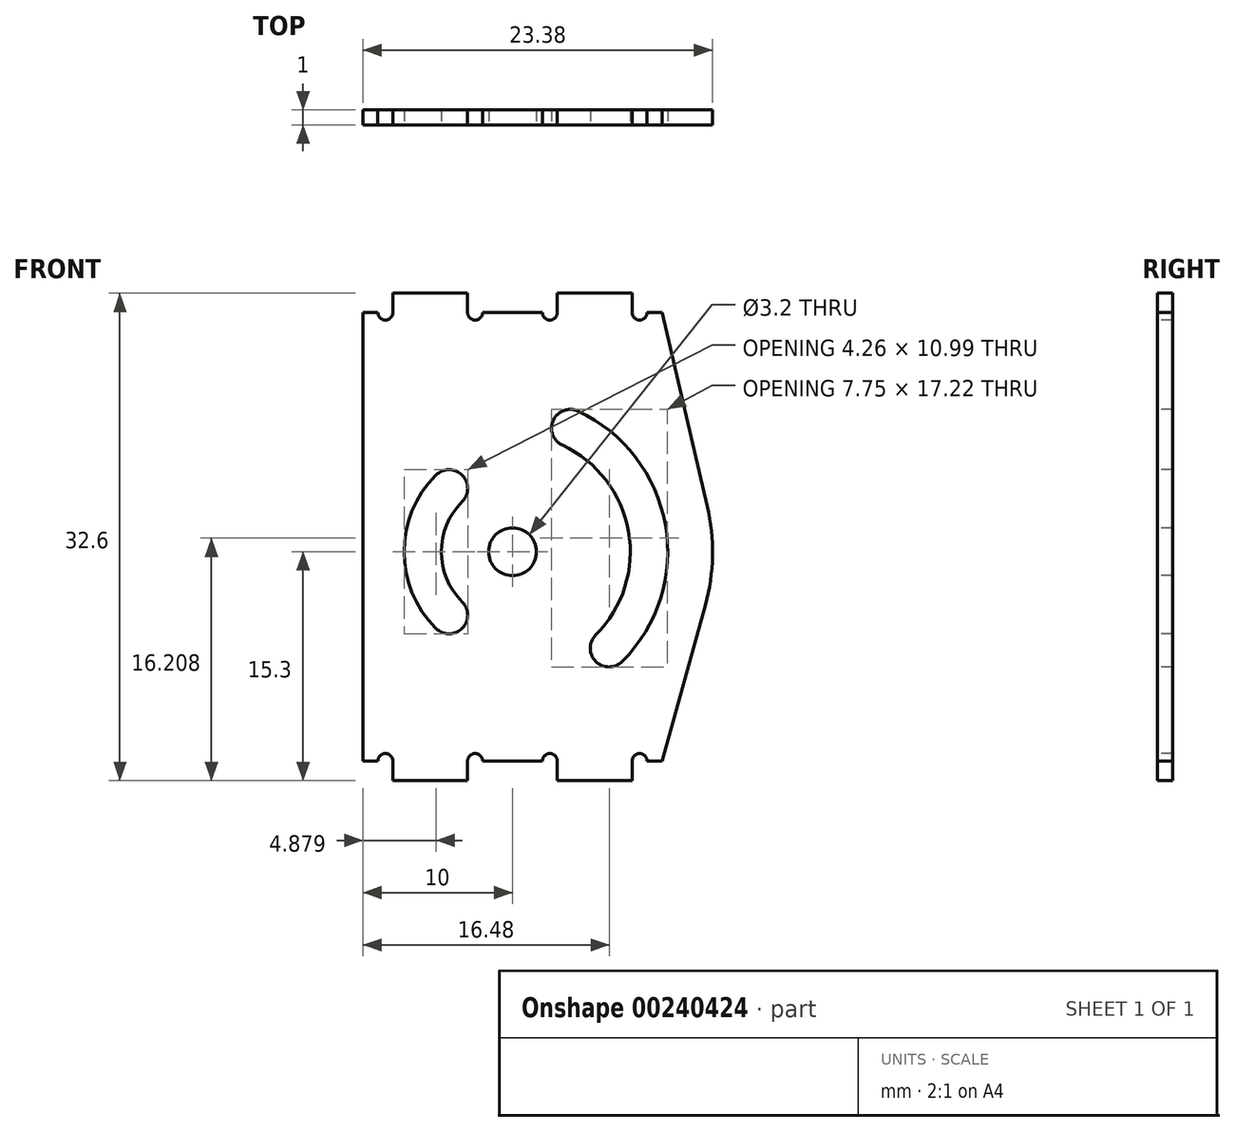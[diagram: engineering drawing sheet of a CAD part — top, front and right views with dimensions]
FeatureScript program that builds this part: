
annotation { "Feature Type Name" : "Feature", "Feature Type Description" : "" }
export const myFeature = defineFeature(function(context is Context, id is Id, definition is map)
    precondition{}
    {
        {
            var Q0;
            Q0=qCreatedBy(makeId("Front.planeOp"),FACE);
            var sketch = newSketch(context, id + "F0", { "sketchPlane" : qUnion([Q0])});
            skLineSegment(sketch, "E0", {"start": v(0, 30) * mm, "end": v(2, 30) * mm});
            skLineSegment(sketch, "E1", {"start": v(0, 30) * mm, "end": v(0, 0) * mm});
            skLineSegment(sketch, "E2", {"start": v(0, 0) * mm, "end": v(2, 0) * mm});
            skLineSegment(sketch, "E3", {"start": v(25, 0) * mm, "end": v(25, 30) * mm});
            skLineSegment(sketch, "E4.top", {"start": v(2, 31.3) * mm, "end": v(7, 31.3) * mm});
            skLineSegment(sketch, "E4.left", {"start": v(2, 30) * mm, "end": v(2, 31.3) * mm});
            skLineSegment(sketch, "E4.right", {"start": v(7, 30) * mm, "end": v(7, 31.3) * mm});
            skLineSegment(sketch, "E5.top", {"start": v(13, 31.3) * mm, "end": v(18, 31.3) * mm});
            skLineSegment(sketch, "E5.left", {"start": v(13, 30) * mm, "end": v(13, 31.3) * mm});
            skLineSegment(sketch, "E5.right", {"start": v(18, 30) * mm, "end": v(18, 31.3) * mm});
            skLineSegment(sketch, "E6.top", {"start": v(2, -1.3) * mm, "end": v(7, -1.3) * mm});
            skLineSegment(sketch, "E6.left", {"start": v(2, 0) * mm, "end": v(2, -1.3) * mm});
            skLineSegment(sketch, "E6.right", {"start": v(7, 0) * mm, "end": v(7, -1.3) * mm});
            skLineSegment(sketch, "E7.trimOffspring", {"start": v(7, 30) * mm, "end": v(13, 30) * mm});
            skLineSegment(sketch, "E8.trimOffspring", {"start": v(18, 30) * mm, "end": v(25, 30) * mm});
            skLineSegment(sketch, "E9", {"start": v(7, 0) * mm, "end": v(13, 0) * mm});
            skLineSegment(sketch, "E10", {"start": v(13, 0) * mm, "end": v(13, -1.3) * mm});
            skLineSegment(sketch, "E11", {"start": v(13, -1.3) * mm, "end": v(18, -1.3) * mm});
            skLineSegment(sketch, "E12", {"start": v(18, -1.3) * mm, "end": v(18, 0) * mm});
            skLineSegment(sketch, "E13", {"start": v(18, 0) * mm, "end": v(25, 0) * mm});
            skSolve(sketch);
        }
        {
            var Q0;
            Q0 = qSketchRegion(id + "F0", true);
            extrude(context, id + "F1", {"entities" : qUnion([Q0]), "depth" : 1 * mm});
        }
        {
            var Q0;
            Q0=makeQuery(id+"F1.opExtrude","CAP_FACE",FACE,{"disambiguationData":[OSD([sQuery(id+"F0.wireOp",EDGE,"E0"),sQuery(id+"F0.wireOp",EDGE,"E1"),sQuery(id+"F0.wireOp",EDGE,"E2"),sQuery(id+"F0.wireOp",EDGE,"Wc9qqe5G-nvfG-rqbr-X8KQ-KRJGeo0Io3PI"),sQuery(id+"F0.wireOp",EDGE,"E3"),sQuery(id+"F0.wireOp",EDGE,"E4.top"),sQuery(id+"F0.wireOp",EDGE,"E4.left"),sQuery(id+"F0.wireOp",EDGE,"E4.right"),sQuery(id+"F0.wireOp",EDGE,"E5.top"),sQuery(id+"F0.wireOp",EDGE,"E5.left"),sQuery(id+"F0.wireOp",EDGE,"E5.right"),sQuery(id+"F0.wireOp",EDGE,"E6.top"),sQuery(id+"F0.wireOp",EDGE,"E6.left"),sQuery(id+"F0.wireOp",EDGE,"E6.right"),sQuery(id+"F0.wireOp",EDGE,"031b728e-5fc7-426f-9de0-9cedf41b9024.trimOffspring"),sQuery(id+"F0.wireOp",EDGE,"E7.trimOffspring"),sQuery(id+"F0.wireOp",EDGE,"E8.trimOffspring")])],"isStart":false});
            var sketch = newSketch(context, id + "F2", { "sketchPlane" : qUnion([Q0])});
            skCircle(sketch, "E14", {"center": v(10, 14) * mm, "radius": 1.6 * mm});
            skArc(sketch, "E15", {"start": v(15.57, 8.43) * mm, "mid": v(17.76, 15.37) * mm, "end": v(13.33, 21.14) * mm});
            skArc(sketch, "E16", {"start": v(17.34, 6.66) * mm, "mid": v(20.22, 15.8) * mm, "end": v(14.38, 23.4) * mm});
            skArc(sketch, "E17", {"start": v(14.38, 23.4) * mm, "mid": v(12.72, 22.8) * mm, "end": v(13.33, 21.14) * mm});
            skArc(sketch, "E18", {"start": v(15.57, 8.43) * mm, "mid": v(15.57, 6.66) * mm, "end": v(17.34, 6.66) * mm});
            skArc(sketch, "E19", {"start": v(15.51, 6.73) * mm, "mid": v(18.99, 15.58) * mm, "end": v(12.69, 22.72) * mm, "construction": true});
            skLineSegment(sketch, "E20", {"start": v(10, 14) * mm, "end": v(13.86, 22.27) * mm, "construction": true});
            skLineSegment(sketch, "E21", {"start": v(10, 14) * mm, "end": v(16.45, 7.55) * mm, "construction": true});
            skLineSegment(sketch, "E22", {"start": v(10, 14) * mm, "end": v(25.4, 14) * mm, "construction": true});
            skArc(sketch, "E23", {"start": v(6.64, 17.36) * mm, "mid": v(5.25, 14) * mm, "end": v(6.64, 10.64) * mm});
            skArc(sketch, "E24", {"start": v(4.87, 19.13) * mm, "mid": v(2.75, 14) * mm, "end": v(4.87, 8.87) * mm});
            skArc(sketch, "E25", {"start": v(4.87, 8.87) * mm, "mid": v(6.64, 8.87) * mm, "end": v(6.64, 10.64) * mm});
            skArc(sketch, "E26", {"start": v(6.64, 17.36) * mm, "mid": v(6.64, 19.13) * mm, "end": v(4.87, 19.13) * mm});
            skArc(sketch, "E27", {"start": v(6.73, 19.03) * mm, "mid": v(4, 14) * mm, "end": v(6.73, 8.97) * mm, "construction": true});
            skLineSegment(sketch, "E28", {"start": v(10, 14) * mm, "end": v(5.76, 9.76) * mm, "construction": true});
            skLineSegment(sketch, "E29", {"start": v(10, 14) * mm, "end": v(5.76, 18.24) * mm, "construction": true});
            skSolve(sketch);
        }
        {
            var Q0;
            Q0 = qSketchRegion(id + "F2", true);
            extrude(context, id + "F3", {"entities" : qUnion([Q0]), "operationType" : NewBodyOperationType.REMOVE, "endBound" : BoundingType.THROUGH_ALL, "oppositeDirection" : true, "depth" : 25 * mm});
        }
        {
            var Q0;
            Q0=makeQuery(id+"F1.opExtrude","CAP_FACE",FACE,{"disambiguationData":[OSD([sQuery(id+"F0.wireOp",EDGE,"E0"),sQuery(id+"F0.wireOp",EDGE,"E1"),sQuery(id+"F0.wireOp",EDGE,"E2"),sQuery(id+"F0.wireOp",EDGE,"Wc9qqe5G-nvfG-rqbr-X8KQ-KRJGeo0Io3PI"),sQuery(id+"F0.wireOp",EDGE,"E3"),sQuery(id+"F0.wireOp",EDGE,"E4.top"),sQuery(id+"F0.wireOp",EDGE,"E4.left"),sQuery(id+"F0.wireOp",EDGE,"E4.right"),sQuery(id+"F0.wireOp",EDGE,"E5.top"),sQuery(id+"F0.wireOp",EDGE,"E5.left"),sQuery(id+"F0.wireOp",EDGE,"E5.right"),sQuery(id+"F0.wireOp",EDGE,"E6.top"),sQuery(id+"F0.wireOp",EDGE,"E6.left"),sQuery(id+"F0.wireOp",EDGE,"E6.right"),sQuery(id+"F0.wireOp",EDGE,"031b728e-5fc7-426f-9de0-9cedf41b9024.trimOffspring"),sQuery(id+"F0.wireOp",EDGE,"E7.trimOffspring"),sQuery(id+"F0.wireOp",EDGE,"E8.trimOffspring")])],"isStart":false});
            var sketch = newSketch(context, id + "F4", { "sketchPlane" : qUnion([Q0])});
            skCircle(sketch, "E30", {"center": v(1.5, 30) * mm, "radius": 0.5 * mm});
            skCircle(sketch, "E31", {"center": v(7.5, 30) * mm, "radius": 0.5 * mm});
            skCircle(sketch, "E32", {"center": v(12.5, 30) * mm, "radius": 0.5 * mm});
            skCircle(sketch, "E33", {"center": v(18.5, 30) * mm, "radius": 0.5 * mm});
            skCircle(sketch, "E34", {"center": v(1.5, 0) * mm, "radius": 0.5 * mm});
            skCircle(sketch, "E35", {"center": v(7.5, 0) * mm, "radius": 0.5 * mm});
            skCircle(sketch, "E36", {"center": v(12.5, 0) * mm, "radius": 0.5 * mm});
            skCircle(sketch, "E37", {"center": v(18.5, 0) * mm, "radius": 0.5 * mm});
            skSolve(sketch);
        }
        {
            var Q0;
            Q0 = qSketchRegion(id + "F4", true);
            extrude(context, id + "F5", {"entities" : qUnion([Q0]), "operationType" : NewBodyOperationType.REMOVE, "endBound" : BoundingType.THROUGH_ALL, "oppositeDirection" : true, "depth" : 25 * mm});
        }
        {
            var Q0;
            Q0=makeQuery(id+"F1.opExtrude","CAP_FACE",FACE,{"disambiguationData":[OSD([sQuery(id+"F0.wireOp",EDGE,"E0"),sQuery(id+"F0.wireOp",EDGE,"E1"),sQuery(id+"F0.wireOp",EDGE,"E2"),sQuery(id+"F0.wireOp",EDGE,"E3"),sQuery(id+"F0.wireOp",EDGE,"E4.top"),sQuery(id+"F0.wireOp",EDGE,"E4.left"),sQuery(id+"F0.wireOp",EDGE,"E4.right"),sQuery(id+"F0.wireOp",EDGE,"E5.top"),sQuery(id+"F0.wireOp",EDGE,"E5.left"),sQuery(id+"F0.wireOp",EDGE,"E5.right"),sQuery(id+"F0.wireOp",EDGE,"E6.top"),sQuery(id+"F0.wireOp",EDGE,"E6.left"),sQuery(id+"F0.wireOp",EDGE,"E6.right"),sQuery(id+"F0.wireOp",EDGE,"E7.trimOffspring"),sQuery(id+"F0.wireOp",EDGE,"E8.trimOffspring"),sQuery(id+"F0.wireOp",EDGE,"E9"),sQuery(id+"F0.wireOp",EDGE,"E10"),sQuery(id+"F0.wireOp",EDGE,"E11"),sQuery(id+"F0.wireOp",EDGE,"E12"),sQuery(id+"F0.wireOp",EDGE,"E13")])],"isStart":false});
            var sketch = newSketch(context, id + "F6", { "sketchPlane" : qUnion([Q0])});
            skLineSegment(sketch, "E38", {"start": v(25, 0) * mm, "end": v(20, 0) * mm});
            skArc(sketch, "E39", {"start": v(22.89, 10.43) * mm, "mid": v(23.37, 13.73) * mm, "end": v(23.02, 17.04) * mm});
            skLineSegment(sketch, "E40", {"start": v(20, 30) * mm, "end": v(23.02, 17.04) * mm});
            skLineSegment(sketch, "E41", {"start": v(20, 0) * mm, "end": v(22.89, 10.43) * mm});
            skLineSegment(sketch, "E42.0", {"start": v(20, 30) * mm, "end": v(25, 30) * mm});
            skLineSegment(sketch, "E43.0", {"start": v(25, 0) * mm, "end": v(25, 30) * mm});
            skPoint(sketch, "E44.orphan", {"position": v(19, 30) * mm});
            skSolve(sketch);
        }
        {
            var Q0;
            Q0 = qSketchRegion(id + "F6", true);
            extrude(context, id + "F7", {"entities" : qUnion([Q0]), "operationType" : NewBodyOperationType.REMOVE, "endBound" : BoundingType.THROUGH_ALL, "oppositeDirection" : true, "depth" : 25 * mm});
        }
    });
